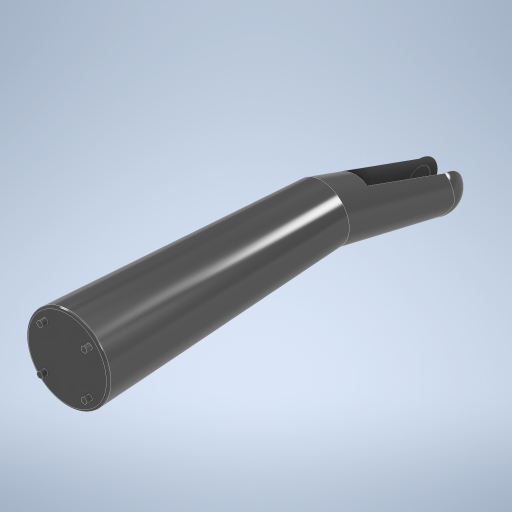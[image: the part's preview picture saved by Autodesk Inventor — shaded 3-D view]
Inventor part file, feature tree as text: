
AUTODESK INVENTOR PART (.ipt)
format: ipt  version: 2023 (Build 270158000, 158)  size: 333,312 bytes
history: native  units: mm
features: sketch x9, other x4, extrude x4, loft x2, revolve x1, fillet x1, projected_geometry x1
ambient origin geometry x8: Origin, YZ Plane, XZ Plane, XY Plane, X Axis, Y Axis, Z Axis, Center Point
bodies: Body1 (feature_tree)
feature tree (22):
  sketch  "스케치1"
  other  "작업 평면1"
  sketch  "스케치3"
  sketch  "스케치2"
  loft  "로프트7"
  other  "작업 평면4"
  loft  "로프트8"
  revolve  "회전2"
  extrude  "돌출1"  Depth=50.0mm
  sketch  "스케치11"
  extrude  "돌출2"  TaperAngle=0.0deg  [1 undecoded]
  extrude  "돌출4"  TaperAngle=0.0deg  [1 undecoded]
  sketch  "스케치18"
  other  "작업 평면5"
  extrude  "돌출7"  Depth=100.0mm
  fillet  "모깎기1"  Radius=40.0mm
  sketch  "스케치7"
  other  "모서리4"
  sketch  "스케치8"
  sketch  "스케치9"
  projected_geometry  "투영된 루프3"
  sketch  "스케치19"
note: 2 required parameter values undecoded (feature->parameter linkage not recoverable at this tier; creation-order binding heuristic only, values carry confidence <= 0.55)
